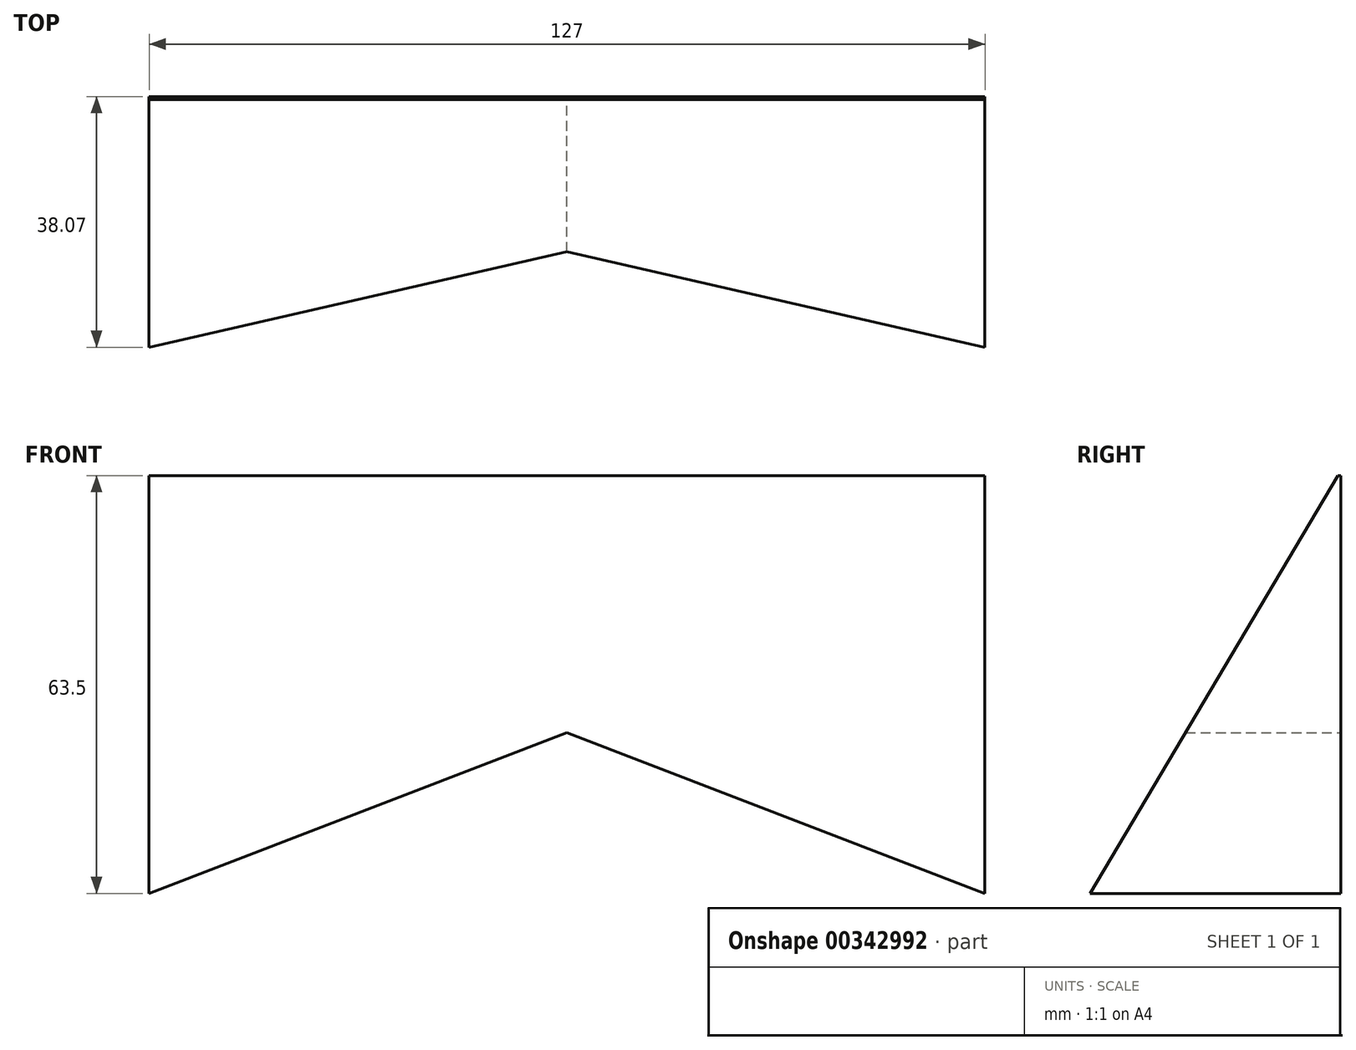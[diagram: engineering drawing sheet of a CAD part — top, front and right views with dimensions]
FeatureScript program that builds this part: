
annotation { "Feature Type Name" : "Feature", "Feature Type Description" : "" }
export const myFeature = defineFeature(function(context is Context, id is Id, definition is map)
    precondition{}
    {
        {
            var Q0;
            Q0=qCreatedBy(makeId("Front.planeOp"),FACE);
            var sketch = newSketch(context, id + "F0", { "sketchPlane" : qUnion([Q0])});
            skLineSegment(sketch, "E0", {"start": v(-67.74, 39.06) * mm, "end": v(59.26, 39.06) * mm});
            skLineSegment(sketch, "E1", {"start": v(59.26, 39.06) * mm, "end": v(59.26, -24.44) * mm});
            skLineSegment(sketch, "E2", {"start": v(-67.74, 39.06) * mm, "end": v(-67.74, -24.44) * mm});
            skLineSegment(sketch, "E3", {"start": v(-67.74, -24.44) * mm, "end": v(-4.24, 0) * mm});
            skLineSegment(sketch, "E4", {"start": v(59.26, -24.44) * mm, "end": v(-4.24, 0) * mm});
            skLineSegment(sketch, "E5", {"start": v(-67.74, 39.06) * mm, "end": v(-4.24, 39.06) * mm});
            skSolve(sketch);
        }
        {
            var Q0;
            Q0=makeQuery(id+"F0.imprint","IMPRINT",FACE,{"disambiguationData":[TD([[makeQuery(id+"F0.imprint","IMPRINT",EDGE,{"derivedFrom":sQuery(id+"F0.wireOp",EDGE,"E0")}),-1.0]])]});
            extrude(context, id + "F1", {"entities" : qUnion([Q0]), "depth" : 38.1 * mm});
        }
        {
            var Q0;
            Q0=qCreatedBy(makeId("Right.planeOp"),FACE);
            var sketch = newSketch(context, id + "F2", { "sketchPlane" : qUnion([Q0])});
            skLineSegment(sketch, "E6", {"start": v(-38.18, 39.79) * mm, "end": v(-38.18, -24.63) * mm});
            skLineSegment(sketch, "E7", {"start": v(-38.18, -24.63) * mm, "end": v(-38.18, 39.79) * mm});
            skLineSegment(sketch, "E8", {"start": v(-38.18, 39.79) * mm, "end": v(0, 39.79) * mm});
            skLineSegment(sketch, "E9", {"start": v(0, 39.79) * mm, "end": v(-38.18, -24.63) * mm});
            skSolve(sketch);
        }
        {
            var Q0;
            Q0 = qSketchRegion(id + "F2", true);
            extrude(context, id + "F3", {"entities" : qUnion([Q0]), "operationType" : NewBodyOperationType.REMOVE, "depth" : 208.53 * mm, "hasSecondDirection" : true, "secondDirectionOppositeDirection" : true, "secondDirectionDepth" : 250.2 * mm});
        }
    });
